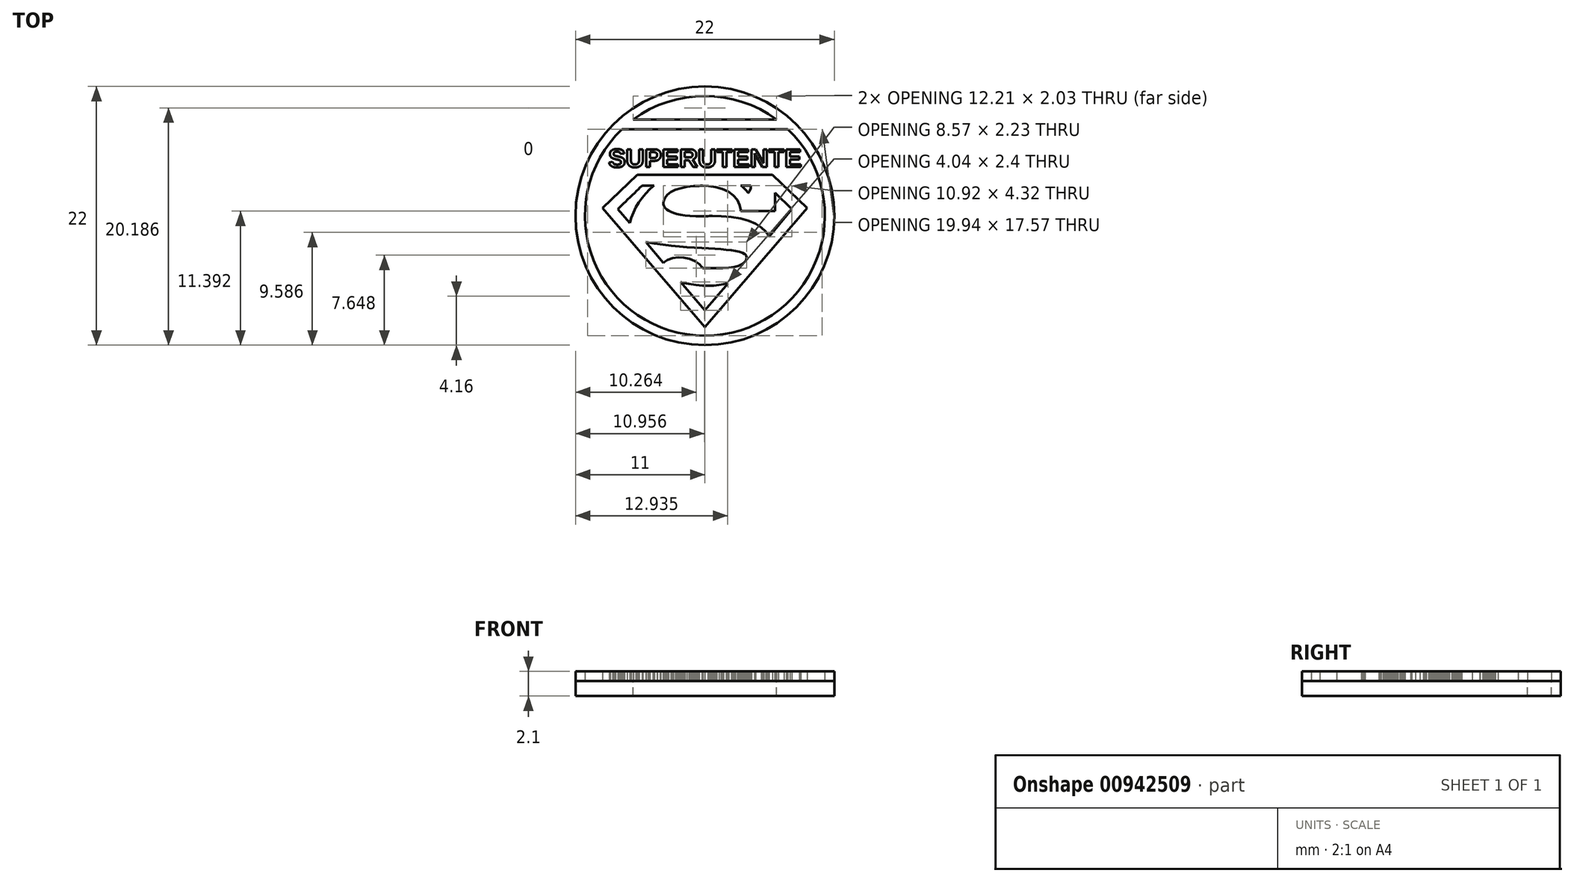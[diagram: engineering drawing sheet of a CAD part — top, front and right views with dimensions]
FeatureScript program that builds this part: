
annotation { "Feature Type Name" : "Feature", "Feature Type Description" : "" }
export const myFeature = defineFeature(function(context is Context, id is Id, definition is map)
    precondition{}
    {
        {
            var Q0;
            Q0=qCreatedBy(makeId("Top.planeOp"),FACE);
            var sketch = newSketch(context, id + "F0", { "sketchPlane" : qUnion([Q0])});
            skLineSegment(sketch, "E0", {"start": v(0, -6.48) * mm, "end": v(-8.69, 3.65) * mm});
            skLineSegment(sketch, "E1", {"start": v(-8.69, 3.65) * mm, "end": v(-5.75, 6.48) * mm});
            skLineSegment(sketch, "E2", {"start": v(-5.75, 6.48) * mm, "end": v(5.75, 6.48) * mm});
            skLineSegment(sketch, "E3", {"start": v(5.75, 6.48) * mm, "end": v(8.69, 3.65) * mm});
            skLineSegment(sketch, "E4", {"start": v(8.69, 3.65) * mm, "end": v(0, -6.48) * mm});
            skLineSegment(sketch, "E5", {"start": v(-5.02, 0.76) * mm, "end": v(-3.53, -1) * mm});
            skLineSegment(sketch, "E6", {"start": v(-3.53, -1) * mm, "end": v(-3.45, -0.93) * mm});
            skLineSegment(sketch, "E7", {"start": v(-3.45, -0.93) * mm, "end": v(-3.18, -0.76) * mm});
            skLineSegment(sketch, "E8", {"start": v(-3.18, -0.76) * mm, "end": v(-2.75, -0.6) * mm});
            skLineSegment(sketch, "E9", {"start": v(-2.75, -0.6) * mm, "end": v(-2.27, -0.54) * mm});
            skLineSegment(sketch, "E10", {"start": v(-2.27, -0.54) * mm, "end": v(-1.78, -0.56) * mm});
            skLineSegment(sketch, "E11", {"start": v(-1.78, -0.56) * mm, "end": v(-1.3, -0.66) * mm});
            skLineSegment(sketch, "E12", {"start": v(-1.3, -0.66) * mm, "end": v(-0.85, -0.84) * mm});
            skLineSegment(sketch, "E13", {"start": v(-0.85, -0.84) * mm, "end": v(-0.47, -1.1) * mm});
            skLineSegment(sketch, "E14", {"start": v(-0.47, -1.1) * mm, "end": v(-0.25, -1.35) * mm});
            skLineSegment(sketch, "E15", {"start": v(-0.25, -1.35) * mm, "end": v(-0.2, -1.45) * mm});
            skLineSegment(sketch, "E16", {"start": v(-0.2, -1.45) * mm, "end": v(-0.04, -1.45) * mm});
            skLineSegment(sketch, "E17", {"start": v(-0.04, -1.45) * mm, "end": v(0.42, -1.46) * mm});
            skLineSegment(sketch, "E18", {"start": v(0.42, -1.46) * mm, "end": v(1, -1.47) * mm});
            skLineSegment(sketch, "E19", {"start": v(1, -1.47) * mm, "end": v(1.53, -1.46) * mm});
            skLineSegment(sketch, "E20", {"start": v(1.53, -1.46) * mm, "end": v(2.03, -1.43) * mm});
            skLineSegment(sketch, "E21", {"start": v(2.03, -1.43) * mm, "end": v(2.47, -1.37) * mm});
            skLineSegment(sketch, "E22", {"start": v(2.47, -1.37) * mm, "end": v(2.86, -1.26) * mm});
            skLineSegment(sketch, "E23", {"start": v(2.86, -1.26) * mm, "end": v(3.17, -1.1) * mm});
            skLineSegment(sketch, "E24", {"start": v(3.17, -1.1) * mm, "end": v(3.37, -0.96) * mm});
            skLineSegment(sketch, "E25", {"start": v(3.37, -0.96) * mm, "end": v(3.42, -0.9) * mm});
            skLineSegment(sketch, "E26", {"start": v(3.42, -0.9) * mm, "end": v(3.44, -0.86) * mm});
            skLineSegment(sketch, "E27", {"start": v(3.44, -0.86) * mm, "end": v(3.51, -0.73) * mm});
            skLineSegment(sketch, "E28", {"start": v(3.51, -0.73) * mm, "end": v(3.55, -0.56) * mm});
            skLineSegment(sketch, "E29", {"start": v(3.55, -0.56) * mm, "end": v(3.52, -0.4) * mm});
            skLineSegment(sketch, "E30", {"start": v(3.52, -0.4) * mm, "end": v(3.44, -0.3) * mm});
            skLineSegment(sketch, "E31", {"start": v(3.44, -0.3) * mm, "end": v(3.41, -0.27) * mm});
            skLineSegment(sketch, "E32", {"start": v(3.41, -0.27) * mm, "end": v(3.36, -0.24) * mm});
            skLineSegment(sketch, "E33", {"start": v(3.36, -0.24) * mm, "end": v(3.2, -0.16) * mm});
            skLineSegment(sketch, "E34", {"start": v(3.2, -0.16) * mm, "end": v(2.93, -0.07) * mm});
            skLineSegment(sketch, "E35", {"start": v(2.93, -0.07) * mm, "end": v(2.6, 0) * mm});
            skLineSegment(sketch, "E36", {"start": v(2.6, 0) * mm, "end": v(2.23, 0.07) * mm});
            skLineSegment(sketch, "E37", {"start": v(2.23, 0.07) * mm, "end": v(1.81, 0.12) * mm});
            skLineSegment(sketch, "E38", {"start": v(1.81, 0.12) * mm, "end": v(1.35, 0.16) * mm});
            skLineSegment(sketch, "E39", {"start": v(1.35, 0.16) * mm, "end": v(0.85, 0.2) * mm});
            skLineSegment(sketch, "E40", {"start": v(0.85, 0.2) * mm, "end": v(0.3, 0.22) * mm});
            skLineSegment(sketch, "E41", {"start": v(0.3, 0.22) * mm, "end": v(-0.27, 0.26) * mm});
            skLineSegment(sketch, "E42", {"start": v(-0.27, 0.26) * mm, "end": v(-0.88, 0.3) * mm});
            skLineSegment(sketch, "E43", {"start": v(-0.88, 0.3) * mm, "end": v(-1.52, 0.34) * mm});
            skLineSegment(sketch, "E44", {"start": v(-1.52, 0.34) * mm, "end": v(-2.18, 0.4) * mm});
            skLineSegment(sketch, "E45", {"start": v(-2.18, 0.4) * mm, "end": v(-2.86, 0.46) * mm});
            skLineSegment(sketch, "E46", {"start": v(-2.86, 0.46) * mm, "end": v(-3.57, 0.54) * mm});
            skLineSegment(sketch, "E47", {"start": v(-3.57, 0.54) * mm, "end": v(-4.29, 0.64) * mm});
            skLineSegment(sketch, "E48", {"start": v(-4.29, 0.64) * mm, "end": v(-4.84, 0.73) * mm});
            skLineSegment(sketch, "E49", {"start": v(-4.84, 0.73) * mm, "end": v(-5.02, 0.76) * mm});
            skLineSegment(sketch, "E50", {"start": v(-7.4, 3.57) * mm, "end": v(-7.38, 3.59) * mm});
            skLineSegment(sketch, "E51", {"start": v(-7.38, 3.59) * mm, "end": v(-7.31, 3.65) * mm});
            skLineSegment(sketch, "E52", {"start": v(-7.31, 3.65) * mm, "end": v(-7.21, 3.75) * mm});
            skLineSegment(sketch, "E53", {"start": v(-7.21, 3.75) * mm, "end": v(-7.08, 3.88) * mm});
            skLineSegment(sketch, "E54", {"start": v(-7.08, 3.88) * mm, "end": v(-6.93, 4.03) * mm});
            skLineSegment(sketch, "E55", {"start": v(-6.93, 4.03) * mm, "end": v(-6.75, 4.2) * mm});
            skLineSegment(sketch, "E56", {"start": v(-6.75, 4.2) * mm, "end": v(-6.56, 4.38) * mm});
            skLineSegment(sketch, "E57", {"start": v(-6.56, 4.38) * mm, "end": v(-6.37, 4.57) * mm});
            skLineSegment(sketch, "E58", {"start": v(-6.37, 4.57) * mm, "end": v(-6.18, 4.76) * mm});
            skLineSegment(sketch, "E59", {"start": v(-6.18, 4.76) * mm, "end": v(-5.99, 4.94) * mm});
            skLineSegment(sketch, "E60", {"start": v(-5.99, 4.94) * mm, "end": v(-5.81, 5.11) * mm});
            skLineSegment(sketch, "E61", {"start": v(-5.81, 5.11) * mm, "end": v(-5.65, 5.26) * mm});
            skLineSegment(sketch, "E62", {"start": v(-5.65, 5.26) * mm, "end": v(-5.52, 5.4) * mm});
            skLineSegment(sketch, "E63", {"start": v(-5.52, 5.4) * mm, "end": v(-5.42, 5.5) * mm});
            skLineSegment(sketch, "E64", {"start": v(-5.42, 5.5) * mm, "end": v(-5.35, 5.56) * mm});
            skLineSegment(sketch, "E65", {"start": v(-5.35, 5.56) * mm, "end": v(-5.33, 5.58) * mm});
            skLineSegment(sketch, "E66", {"start": v(-5.33, 5.58) * mm, "end": v(-4.32, 5.58) * mm});
            skLineSegment(sketch, "E67", {"start": v(-4.32, 5.58) * mm, "end": v(-4.41, 5.5) * mm});
            skLineSegment(sketch, "E68", {"start": v(-4.41, 5.5) * mm, "end": v(-4.69, 5.25) * mm});
            skLineSegment(sketch, "E69", {"start": v(-4.69, 5.25) * mm, "end": v(-5.03, 4.9) * mm});
            skLineSegment(sketch, "E70", {"start": v(-5.03, 4.9) * mm, "end": v(-5.34, 4.53) * mm});
            skLineSegment(sketch, "E71", {"start": v(-5.34, 4.53) * mm, "end": v(-5.62, 4.13) * mm});
            skLineSegment(sketch, "E72", {"start": v(-5.62, 4.13) * mm, "end": v(-5.86, 3.72) * mm});
            skLineSegment(sketch, "E73", {"start": v(-5.86, 3.72) * mm, "end": v(-6.08, 3.28) * mm});
            skLineSegment(sketch, "E74", {"start": v(-6.08, 3.28) * mm, "end": v(-6.25, 2.84) * mm});
            skLineSegment(sketch, "E75", {"start": v(-6.25, 2.84) * mm, "end": v(-6.36, 2.5) * mm});
            skLineSegment(sketch, "E76", {"start": v(-6.36, 2.5) * mm, "end": v(-6.39, 2.38) * mm});
            skLineSegment(sketch, "E77", {"start": v(-6.39, 2.38) * mm, "end": v(-7.4, 3.57) * mm});
            skLineSegment(sketch, "E78", {"start": v(-2.07, -2.64) * mm, "end": v(0, -5.04) * mm});
            skLineSegment(sketch, "E79", {"start": v(0, -5.04) * mm, "end": v(1.98, -2.74) * mm});
            skLineSegment(sketch, "E80", {"start": v(1.98, -2.74) * mm, "end": v(1.88, -2.76) * mm});
            skLineSegment(sketch, "E81", {"start": v(1.88, -2.76) * mm, "end": v(1.6, -2.82) * mm});
            skLineSegment(sketch, "E82", {"start": v(1.6, -2.82) * mm, "end": v(1.2, -2.89) * mm});
            skLineSegment(sketch, "E83", {"start": v(1.2, -2.89) * mm, "end": v(0.76, -2.93) * mm});
            skLineSegment(sketch, "E84", {"start": v(0.76, -2.93) * mm, "end": v(0.3, -2.95) * mm});
            skLineSegment(sketch, "E85", {"start": v(0.3, -2.95) * mm, "end": v(-0.2, -2.93) * mm});
            skLineSegment(sketch, "E86", {"start": v(-0.2, -2.93) * mm, "end": v(-0.76, -2.88) * mm});
            skLineSegment(sketch, "E87", {"start": v(-0.76, -2.88) * mm, "end": v(-1.38, -2.78) * mm});
            skLineSegment(sketch, "E88", {"start": v(-1.38, -2.78) * mm, "end": v(-1.9, -2.68) * mm});
            skLineSegment(sketch, "E89", {"start": v(-1.9, -2.68) * mm, "end": v(-2.07, -2.64) * mm});
            skLineSegment(sketch, "E90", {"start": v(3.04, 5.58) * mm, "end": v(3.91, 5.58) * mm});
            skLineSegment(sketch, "E91", {"start": v(3.91, 5.58) * mm, "end": v(3.91, 5.52) * mm});
            skLineSegment(sketch, "E92", {"start": v(3.91, 5.52) * mm, "end": v(3.9, 5.36) * mm});
            skLineSegment(sketch, "E93", {"start": v(3.9, 5.36) * mm, "end": v(3.84, 5.18) * mm});
            skLineSegment(sketch, "E94", {"start": v(3.84, 5.18) * mm, "end": v(3.76, 5.05) * mm});
            skLineSegment(sketch, "E95", {"start": v(3.76, 5.05) * mm, "end": v(3.7, 4.97) * mm});
            skLineSegment(sketch, "E96", {"start": v(3.7, 4.97) * mm, "end": v(3.68, 4.95) * mm});
            skLineSegment(sketch, "E97", {"start": v(3.68, 4.95) * mm, "end": v(3.64, 5) * mm});
            skLineSegment(sketch, "E98", {"start": v(3.64, 5) * mm, "end": v(3.5, 5.16) * mm});
            skLineSegment(sketch, "E99", {"start": v(3.5, 5.16) * mm, "end": v(3.33, 5.35) * mm});
            skLineSegment(sketch, "E100", {"start": v(3.33, 5.35) * mm, "end": v(3.16, 5.5) * mm});
            skLineSegment(sketch, "E101", {"start": v(3.16, 5.5) * mm, "end": v(3.07, 5.56) * mm});
            skLineSegment(sketch, "E102", {"start": v(3.07, 5.56) * mm, "end": v(3.04, 5.58) * mm});
            skLineSegment(sketch, "E103", {"start": v(5.44, 1.23) * mm, "end": v(7.4, 3.57) * mm});
            skLineSegment(sketch, "E104", {"start": v(7.4, 3.57) * mm, "end": v(5.98, 4.97) * mm});
            skLineSegment(sketch, "E105", {"start": v(5.98, 4.97) * mm, "end": v(5.98, 3.4) * mm});
            skLineSegment(sketch, "E106", {"start": v(5.98, 3.4) * mm, "end": v(3.06, 3.4) * mm});
            skLineSegment(sketch, "E107", {"start": v(3.06, 3.4) * mm, "end": v(3.05, 3.53) * mm});
            skLineSegment(sketch, "E108", {"start": v(3.05, 3.53) * mm, "end": v(2.96, 3.92) * mm});
            skLineSegment(sketch, "E109", {"start": v(2.96, 3.92) * mm, "end": v(2.75, 4.38) * mm});
            skLineSegment(sketch, "E110", {"start": v(2.75, 4.38) * mm, "end": v(2.42, 4.75) * mm});
            skLineSegment(sketch, "E111", {"start": v(2.42, 4.75) * mm, "end": v(2, 5.05) * mm});
            skLineSegment(sketch, "E112", {"start": v(2, 5.05) * mm, "end": v(1.5, 5.28) * mm});
            skLineSegment(sketch, "E113", {"start": v(1.5, 5.28) * mm, "end": v(0.93, 5.44) * mm});
            skLineSegment(sketch, "E114", {"start": v(0.93, 5.44) * mm, "end": v(0.3, 5.53) * mm});
            skLineSegment(sketch, "E115", {"start": v(0.3, 5.53) * mm, "end": v(-0.19, 5.55) * mm});
            skLineSegment(sketch, "E116", {"start": v(-0.19, 5.55) * mm, "end": v(-0.35, 5.55) * mm});
            skLineSegment(sketch, "E117", {"start": v(-0.35, 5.55) * mm, "end": v(-0.5, 5.55) * mm});
            skLineSegment(sketch, "E118", {"start": v(-0.5, 5.55) * mm, "end": v(-0.96, 5.53) * mm});
            skLineSegment(sketch, "E119", {"start": v(-0.96, 5.53) * mm, "end": v(-1.52, 5.46) * mm});
            skLineSegment(sketch, "E120", {"start": v(-1.52, 5.46) * mm, "end": v(-2.04, 5.36) * mm});
            skLineSegment(sketch, "E121", {"start": v(-2.04, 5.36) * mm, "end": v(-2.5, 5.21) * mm});
            skLineSegment(sketch, "E122", {"start": v(-2.5, 5.21) * mm, "end": v(-2.89, 5.03) * mm});
            skLineSegment(sketch, "E123", {"start": v(-2.89, 5.03) * mm, "end": v(-3.2, 4.8) * mm});
            skLineSegment(sketch, "E124", {"start": v(-3.2, 4.8) * mm, "end": v(-3.4, 4.52) * mm});
            skLineSegment(sketch, "E125", {"start": v(-3.4, 4.52) * mm, "end": v(-3.5, 4.28) * mm});
            skLineSegment(sketch, "E126", {"start": v(-3.5, 4.28) * mm, "end": v(-3.51, 4.2) * mm});
            skLineSegment(sketch, "E127", {"start": v(-3.51, 4.2) * mm, "end": v(-3.52, 4.17) * mm});
            skLineSegment(sketch, "E128", {"start": v(-3.52, 4.17) * mm, "end": v(-3.53, 4.1) * mm});
            skLineSegment(sketch, "E129", {"start": v(-3.53, 4.1) * mm, "end": v(-3.52, 3.99) * mm});
            skLineSegment(sketch, "E130", {"start": v(-3.52, 3.99) * mm, "end": v(-3.5, 3.88) * mm});
            skLineSegment(sketch, "E131", {"start": v(-3.5, 3.88) * mm, "end": v(-3.44, 3.76) * mm});
            skLineSegment(sketch, "E132", {"start": v(-3.44, 3.76) * mm, "end": v(-3.36, 3.65) * mm});
            skLineSegment(sketch, "E133", {"start": v(-3.36, 3.65) * mm, "end": v(-3.24, 3.54) * mm});
            skLineSegment(sketch, "E134", {"start": v(-3.24, 3.54) * mm, "end": v(-3.1, 3.43) * mm});
            skLineSegment(sketch, "E135", {"start": v(-3.1, 3.43) * mm, "end": v(-2.9, 3.33) * mm});
            skLineSegment(sketch, "E136", {"start": v(-2.9, 3.33) * mm, "end": v(-2.67, 3.23) * mm});
            skLineSegment(sketch, "E137", {"start": v(-2.67, 3.23) * mm, "end": v(-2.4, 3.15) * mm});
            skLineSegment(sketch, "E138", {"start": v(-2.4, 3.15) * mm, "end": v(-2.07, 3.08) * mm});
            skLineSegment(sketch, "E139", {"start": v(-2.07, 3.08) * mm, "end": v(-1.7, 3.02) * mm});
            skLineSegment(sketch, "E140", {"start": v(-1.7, 3.02) * mm, "end": v(-1.26, 2.98) * mm});
            skLineSegment(sketch, "E141", {"start": v(-1.26, 2.98) * mm, "end": v(-0.77, 2.96) * mm});
            skLineSegment(sketch, "E142", {"start": v(-0.77, 2.96) * mm, "end": v(-0.22, 2.96) * mm});
            skLineSegment(sketch, "E143", {"start": v(-0.22, 2.96) * mm, "end": v(0.24, 2.97) * mm});
            skLineSegment(sketch, "E144", {"start": v(0.24, 2.97) * mm, "end": v(0.4, 2.98) * mm});
            skLineSegment(sketch, "E145", {"start": v(0.4, 2.98) * mm, "end": v(0.64, 2.98) * mm});
            skLineSegment(sketch, "E146", {"start": v(0.64, 2.98) * mm, "end": v(1.38, 2.97) * mm});
            skLineSegment(sketch, "E147", {"start": v(1.38, 2.97) * mm, "end": v(2.26, 2.9) * mm});
            skLineSegment(sketch, "E148", {"start": v(2.26, 2.9) * mm, "end": v(3.04, 2.77) * mm});
            skLineSegment(sketch, "E149", {"start": v(3.04, 2.77) * mm, "end": v(3.73, 2.58) * mm});
            skLineSegment(sketch, "E150", {"start": v(3.73, 2.58) * mm, "end": v(4.3, 2.33) * mm});
            skLineSegment(sketch, "E151", {"start": v(4.3, 2.33) * mm, "end": v(4.79, 2.02) * mm});
            skLineSegment(sketch, "E152", {"start": v(4.79, 2.02) * mm, "end": v(5.17, 1.65) * mm});
            skLineSegment(sketch, "E153", {"start": v(5.17, 1.65) * mm, "end": v(5.39, 1.34) * mm});
            skLineSegment(sketch, "E154", {"start": v(5.39, 1.34) * mm, "end": v(5.44, 1.23) * mm});
            skCircle(sketch, "E155", {"center": v(0, 3) * mm, "radius": 11 * mm});
            skArc(sketch, "E156.0", {"start": v(-7.05, 10.37) * mm, "mid": v(0, -7.2) * mm, "end": v(7.05, 10.37) * mm});
            skLineSegment(sketch, "E157.0", {"start": v(-6.1, 11.17) * mm, "end": v(6.1, 11.17) * mm});
            skArc(sketch, "E158.trimOffspring", {"start": v(6.1, 11.17) * mm, "mid": v(0, 13.2) * mm, "end": v(-6.1, 11.17) * mm});
            skText(sketch, "E159", { "text": "SUPERUTENTE", "fontName": "Arimo-Bold.ttf"});
            skLineSegment(sketch, "E160.0", {"start": v(-7.05, 10.37) * mm, "end": v(7.05, 10.37) * mm});
            const initialGuessF0  = {"E159": [-0.00821, 0.00714, 1, 0, 0.00159]};
            skSetInitialGuess(sketch, initialGuessF0);
            skSolve(sketch);
        }
        {
            var Q0;
            Q0=makeQuery(id+"F0.imprint","IMPRINT",FACE,{"disambiguationData":[TD([[makeQuery(id+"F0.imprint","IMPRINT",EDGE,{"derivedFrom":sQuery(id+"F0.wireOp",EDGE,"E155")}),1.0]])]});
            var Q1;
            Q1=makeQuery(id+"F0.imprint","IMPRINT",FACE,{"disambiguationData":[TD([[makeQuery(id+"F0.imprint","IMPRINT",EDGE,{"derivedFrom":sQuery(id+"F0.wireOp",EDGE,"E0")}),1.0]])]});
            var Q2;
            Q2=makeQuery(id+"F0.imprint","IMPRINT",FACE,{"disambiguationData":[TD([[makeQuery(id+"F0.imprint","IMPRINT",EDGE,{"derivedFrom":sQuery(id+"F0.wireOp",EDGE,"E0")}),-1.0]])]});
            var Q3;
            Q3=makeQuery(id+"F0.imprint","IMPRINT",FACE,{"disambiguationData":[TD([[makeQuery(id+"F0.imprint","IMPRINT",EDGE,{"derivedFrom":sQuery(id+"F0.wireOp",EDGE,"E50")}),-1.0]])]});
            var Q4;
            Q4=makeQuery(id+"F0.imprint","IMPRINT",FACE,{"disambiguationData":[TD([[makeQuery(id+"F0.imprint","IMPRINT",EDGE,{"derivedFrom":sQuery(id+"F0.wireOp",EDGE,"E103")}),1.0]])]});
            var Q5;
            Q5=makeQuery(id+"F0.imprint","IMPRINT",FACE,{"disambiguationData":[TD([[makeQuery(id+"F0.imprint","IMPRINT",EDGE,{"derivedFrom":sQuery(id+"F0.wireOp",EDGE,"E5")}),1.0]])]});
            var Q6;
            Q6=makeQuery(id+"F0.imprint","IMPRINT",FACE,{"disambiguationData":[TD([[makeQuery(id+"F0.imprint","IMPRINT",EDGE,{"derivedFrom":sQuery(id+"F0.wireOp",EDGE,"E78")}),1.0]])]});
            var Q7;
            Q7=makeQuery(id+"F0.imprint","IMPRINT",FACE,{"disambiguationData":[TD([[makeQuery(id+"F0.imprint","IMPRINT",EDGE,{"derivedFrom":sQuery(id+"F0.wireOp",EDGE,"E90")}),-1.0]])]});
            var Q8;
            Q8=makeQuery(id+"F0.imprint","IMPRINT",FACE,{"disambiguationData":[TD([[makeQuery(id+"F0.imprint","IMPRINT",EDGE,{"derivedFrom":sQuery(id+"F0.wireOp",EDGE,"E159.sketch_text.stroke-154")}),1.0]])]});
            var Q9;
            Q9=makeQuery(id+"F0.imprint","IMPRINT",FACE,{"disambiguationData":[TD([[makeQuery(id+"F0.imprint","IMPRINT",EDGE,{"derivedFrom":sQuery(id+"F0.wireOp",EDGE,"E159.sketch_text.stroke-142")}),-1.0]])]});
            var Q10;
            Q10=makeQuery(id+"F0.imprint","IMPRINT",FACE,{"disambiguationData":[TD([[makeQuery(id+"F0.imprint","IMPRINT",EDGE,{"derivedFrom":sQuery(id+"F0.wireOp",EDGE,"E159.sketch_text.stroke-160")}),-1.0]])]});
            var Q11;
            Q11=makeQuery(id+"F0.imprint","IMPRINT",FACE,{"disambiguationData":[TD([[makeQuery(id+"F0.imprint","IMPRINT",EDGE,{"derivedFrom":sQuery(id+"F0.wireOp",EDGE,"E159.sketch_text.stroke-125")}),-1.0]])]});
            var Q12;
            Q12=makeQuery(id+"F0.imprint","IMPRINT",FACE,{"disambiguationData":[TD([[makeQuery(id+"F0.imprint","IMPRINT",EDGE,{"derivedFrom":sQuery(id+"F0.wireOp",EDGE,"E159.sketch_text.stroke-134")}),1.0]])]});
            var Q13;
            Q13=makeQuery(id+"F0.imprint","IMPRINT",FACE,{"disambiguationData":[TD([[makeQuery(id+"F0.imprint","IMPRINT",EDGE,{"derivedFrom":sQuery(id+"F0.wireOp",EDGE,"E159.sketch_text.stroke-117")}),-1.0]])]});
            var Q14;
            Q14=makeQuery(id+"F0.imprint","IMPRINT",FACE,{"disambiguationData":[TD([[makeQuery(id+"F0.imprint","IMPRINT",EDGE,{"derivedFrom":sQuery(id+"F0.wireOp",EDGE,"E159.sketch_text.stroke-109")}),-1.0]])]});
            var Q15;
            Q15=makeQuery(id+"F0.imprint","IMPRINT",FACE,{"disambiguationData":[TD([[makeQuery(id+"F0.imprint","IMPRINT",EDGE,{"derivedFrom":sQuery(id+"F0.wireOp",EDGE,"E159.sketch_text.stroke-97")}),-1.0]])]});
            var Q16;
            Q16=makeQuery(id+"F0.imprint","IMPRINT",FACE,{"disambiguationData":[TD([[makeQuery(id+"F0.imprint","IMPRINT",EDGE,{"derivedFrom":sQuery(id+"F0.wireOp",EDGE,"E159.sketch_text.stroke-0")}),-1.0]])]});
            var Q17;
            Q17=makeQuery(id+"F0.imprint","IMPRINT",FACE,{"disambiguationData":[TD([[makeQuery(id+"F0.imprint","IMPRINT",EDGE,{"derivedFrom":sQuery(id+"F0.wireOp",EDGE,"E159.sketch_text.stroke-31")}),-1.0]])]});
            var Q18;
            Q18=makeQuery(id+"F0.imprint","IMPRINT",FACE,{"disambiguationData":[TD([[makeQuery(id+"F0.imprint","IMPRINT",EDGE,{"derivedFrom":sQuery(id+"F0.wireOp",EDGE,"E159.sketch_text.stroke-45")}),-1.0]])]});
            var Q19;
            Q19=makeQuery(id+"F0.imprint","IMPRINT",FACE,{"disambiguationData":[TD([[makeQuery(id+"F0.imprint","IMPRINT",EDGE,{"derivedFrom":sQuery(id+"F0.wireOp",EDGE,"E159.sketch_text.stroke-55")}),1.0]])]});
            var Q20;
            Q20=makeQuery(id+"F0.imprint","IMPRINT",FACE,{"disambiguationData":[TD([[makeQuery(id+"F0.imprint","IMPRINT",EDGE,{"derivedFrom":sQuery(id+"F0.wireOp",EDGE,"E159.sketch_text.stroke-61")}),-1.0]])]});
            var Q21;
            Q21=makeQuery(id+"F0.imprint","IMPRINT",FACE,{"disambiguationData":[TD([[makeQuery(id+"F0.imprint","IMPRINT",EDGE,{"derivedFrom":sQuery(id+"F0.wireOp",EDGE,"E159.sketch_text.stroke-73")}),-1.0]])]});
            var Q22;
            Q22=makeQuery(id+"F0.imprint","IMPRINT",FACE,{"disambiguationData":[TD([[makeQuery(id+"F0.imprint","IMPRINT",EDGE,{"derivedFrom":sQuery(id+"F0.wireOp",EDGE,"E159.sketch_text.stroke-85")}),1.0]])]});
            var Q23;
            Q23=makeQuery(id+"F0.imprint","IMPRINT",FACE,{"disambiguationData":[TD([[makeQuery(id+"F0.imprint","IMPRINT",EDGE,{"derivedFrom":sQuery(id+"F0.wireOp",EDGE,"E159.sketch_text.stroke-91")}),-1.0]])]});
            var Q24;
            Q24=makeQuery(id+"F0.imprint","IMPRINT",FACE,{"disambiguationData":[TD([[makeQuery(id+"F0.imprint","IMPRINT",EDGE,{"derivedFrom":sQuery(id+"F0.wireOp",EDGE,"E159.sketch_text.stroke-145")}),-1.0]])]});
            extrude(context, id + "F1", {"entities" : qUnion([Q0, Q1, Q2, Q3, Q4, Q5, Q6, Q7, Q8, Q9, Q10, Q11, Q12, Q13, Q14, Q15, Q16, Q17, Q18, Q19, Q20, Q21, Q22, Q23, Q24]), "oppositeDirection" : true, "depth" : 1.3 * mm, "offsetDistance" : 25 * mm});
        }
        {
            var Q0;
            Q0=makeQuery(id+"F0.imprint","IMPRINT",FACE,{"disambiguationData":[TD([[makeQuery(id+"F0.imprint","IMPRINT",EDGE,{"derivedFrom":sQuery(id+"F0.wireOp",EDGE,"E159.sketch_text.stroke-0")}),-1.0]])]});
            var Q1;
            Q1=makeQuery(id+"F0.imprint","IMPRINT",FACE,{"disambiguationData":[TD([[makeQuery(id+"F0.imprint","IMPRINT",EDGE,{"derivedFrom":sQuery(id+"F0.wireOp",EDGE,"E159.sketch_text.stroke-31")}),-1.0]])]});
            var Q2;
            Q2=makeQuery(id+"F0.imprint","IMPRINT",FACE,{"disambiguationData":[TD([[makeQuery(id+"F0.imprint","IMPRINT",EDGE,{"derivedFrom":sQuery(id+"F0.wireOp",EDGE,"E159.sketch_text.stroke-45")}),-1.0]])]});
            var Q3;
            Q3=makeQuery(id+"F0.imprint","IMPRINT",FACE,{"disambiguationData":[TD([[makeQuery(id+"F0.imprint","IMPRINT",EDGE,{"derivedFrom":sQuery(id+"F0.wireOp",EDGE,"E159.sketch_text.stroke-61")}),-1.0]])]});
            var Q4;
            Q4=makeQuery(id+"F0.imprint","IMPRINT",FACE,{"disambiguationData":[TD([[makeQuery(id+"F0.imprint","IMPRINT",EDGE,{"derivedFrom":sQuery(id+"F0.wireOp",EDGE,"E159.sketch_text.stroke-73")}),-1.0]])]});
            var Q5;
            Q5=makeQuery(id+"F0.imprint","IMPRINT",FACE,{"disambiguationData":[TD([[makeQuery(id+"F0.imprint","IMPRINT",EDGE,{"derivedFrom":sQuery(id+"F0.wireOp",EDGE,"E159.sketch_text.stroke-91")}),-1.0]])]});
            var Q6;
            Q6=makeQuery(id+"F0.imprint","IMPRINT",FACE,{"disambiguationData":[TD([[makeQuery(id+"F0.imprint","IMPRINT",EDGE,{"derivedFrom":sQuery(id+"F0.wireOp",EDGE,"E159.sketch_text.stroke-97")}),-1.0]])]});
            var Q7;
            Q7=makeQuery(id+"F0.imprint","IMPRINT",FACE,{"disambiguationData":[TD([[makeQuery(id+"F0.imprint","IMPRINT",EDGE,{"derivedFrom":sQuery(id+"F0.wireOp",EDGE,"E159.sketch_text.stroke-109")}),-1.0]])]});
            var Q8;
            Q8=makeQuery(id+"F0.imprint","IMPRINT",FACE,{"disambiguationData":[TD([[makeQuery(id+"F0.imprint","IMPRINT",EDGE,{"derivedFrom":sQuery(id+"F0.wireOp",EDGE,"E159.sketch_text.stroke-117")}),-1.0]])]});
            var Q9;
            Q9=makeQuery(id+"F0.imprint","IMPRINT",FACE,{"disambiguationData":[TD([[makeQuery(id+"F0.imprint","IMPRINT",EDGE,{"derivedFrom":sQuery(id+"F0.wireOp",EDGE,"E159.sketch_text.stroke-125")}),-1.0]])]});
            var Q10;
            Q10=makeQuery(id+"F0.imprint","IMPRINT",FACE,{"disambiguationData":[TD([[makeQuery(id+"F0.imprint","IMPRINT",EDGE,{"derivedFrom":sQuery(id+"F0.wireOp",EDGE,"E159.sketch_text.stroke-142")}),-1.0]])]});
            var Q11;
            Q11=makeQuery(id+"F0.imprint","IMPRINT",FACE,{"disambiguationData":[TD([[makeQuery(id+"F0.imprint","IMPRINT",EDGE,{"derivedFrom":sQuery(id+"F0.wireOp",EDGE,"E159.sketch_text.stroke-160")}),-1.0]])]});
            var Q12;
            Q12=makeQuery(id+"F0.imprint","IMPRINT",FACE,{"disambiguationData":[TD([[makeQuery(id+"F0.imprint","IMPRINT",EDGE,{"derivedFrom":sQuery(id+"F0.wireOp",EDGE,"E155")}),1.0]])]});
            var Q13;
            Q13=makeQuery(id+"F0.imprint","IMPRINT",FACE,{"disambiguationData":[TD([[makeQuery(id+"F0.imprint","IMPRINT",EDGE,{"derivedFrom":sQuery(id+"F0.wireOp",EDGE,"E0")}),-1.0]])]});
            var Q14;
            Q14=makeQuery(id+"F0.imprint","IMPRINT",FACE,{"disambiguationData":[TD([[makeQuery(id+"F0.imprint","IMPRINT",EDGE,{"derivedFrom":sQuery(id+"F0.wireOp",EDGE,"E159.sketch_text.stroke-145")}),-1.0]])]});
            extrude(context, id + "F2", {"entities" : qUnion([Q0, Q1, Q2, Q3, Q4, Q5, Q6, Q7, Q8, Q9, Q10, Q11, Q12, Q13, Q14]), "depth" : .8 * mm, "offsetDistance" : 25 * mm});
        }
    });
